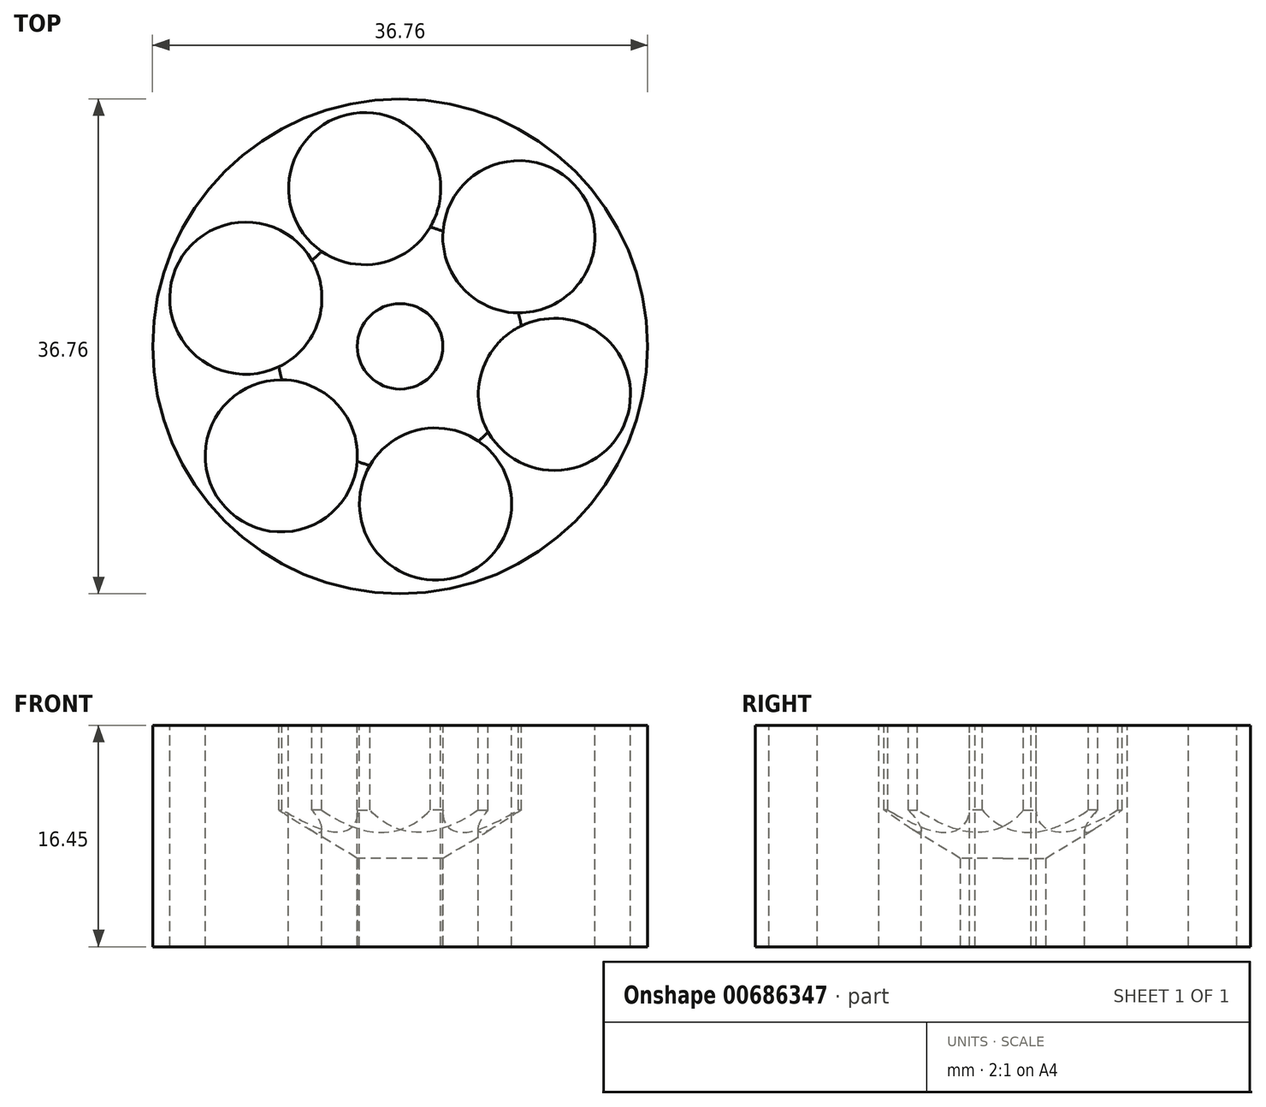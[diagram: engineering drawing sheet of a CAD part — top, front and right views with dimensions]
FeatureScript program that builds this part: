
annotation { "Feature Type Name" : "Feature", "Feature Type Description" : "" }
export const myFeature = defineFeature(function(context is Context, id is Id, definition is map)
    precondition{}
    {
        {
            var Q0;
            Q0=qCreatedBy(makeId("Top.planeOp"),FACE);
            var sketch = newSketch(context, id + "F0", { "sketchPlane" : qUnion([Q0])});
            skCircle(sketch, "E0", {"center": v(0, 0) * mm, "radius": 18.38 * mm});
            skSolve(sketch);
        }
        {
            var Q0;
            Q0=makeQuery(id+"F0.imprint","IMPRINT",FACE,{"disambiguationData":[TD([[makeQuery(id+"F0.imprint","IMPRINT",EDGE,{"derivedFrom":sQuery(id+"F0.wireOp",EDGE,"E0")}),1.0]])]});
            extrude(context, id + "F1", {"entities" : qUnion([Q0]), "depth" : 16.45 * mm, "offsetDistance" : 25.4 * mm});
        }
        {
            var Q0;
            Q0=makeQuery(id+"F1.opExtrude","CAP_FACE",FACE,{"disambiguationData":[OSD([sQuery(id+"F0.wireOp",EDGE,"E0")])],"isStart":false});
            var sketch = newSketch(context, id + "F2", { "sketchPlane" : qUnion([Q0])});
            skCircle(sketch, "E1", {"center": v(0, 0) * mm, "radius": 12 * mm, "construction": true});
            skCircle(sketch, "E2", {"center": v(-11.46, 3.57) * mm, "radius": 4.63 * mm});
            skCircle(sketch, "E3.1.0", {"center": v(-8.82, -8.13) * mm, "radius": 4.63 * mm});
            skCircle(sketch, "E3.2.0", {"center": v(2.63, -11.7) * mm, "radius": 4.63 * mm});
            skCircle(sketch, "E3.3.0", {"center": v(11.46, -3.57) * mm, "radius": 4.63 * mm});
            skCircle(sketch, "E3.4.0", {"center": v(8.82, 8.13) * mm, "radius": 4.63 * mm});
            skCircle(sketch, "E3.5.0", {"center": v(-2.63, 11.7) * mm, "radius": 4.63 * mm});
            skSolve(sketch);
        }
        {
            var Q0;
            Q0=sQuery(id+"F2.wireOp",VERTEX,"E3.1.0.center");
            var Q1;
            Q1=sQuery(id+"F2.wireOp",VERTEX,"E3.5.0.center");
            var Q2;
            Q2=sQuery(id+"F2.wireOp",VERTEX,"E2.center");
            var Q3;
            Q3=sQuery(id+"F2.wireOp",VERTEX,"E3.2.0.center");
            var Q4;
            Q4=sQuery(id+"F2.wireOp",VERTEX,"E3.3.0.center");
            var Q5;
            Q5=sQuery(id+"F2.wireOp",VERTEX,"E3.4.0.center");
            var Q6;
            Q6=makeQuery(id+"F1.opExtrude","SWEPT_BODY",BODY,{"disambiguationData":[OSD([sQuery(id+"F0.wireOp",EDGE,"E0")])]});
            hole(context, id + "F3", {"style" : HoleStyle.SIMPLE, "endStyle" : HoleEndStyle.THROUGH, "holeDiameter" : 11.3 * mm, "majorDiameter" : 6.35 * mm, "isTappedThrough" : true, "tappedDepth" : 12.7 * mm, "tapClearance" : 3, "locations" : qUnion([Q0, Q1, Q2, Q3, Q4, Q5]), "scope" : qUnion([Q6])});
        }
        {
            var Q0;
            Q0=makeQuery(id+"F1.opExtrude","CAP_FACE",FACE,{"disambiguationData":[OSD([sQuery(id+"F0.wireOp",EDGE,"E0")])],"isStart":false});
            var sketch = newSketch(context, id + "F4", { "sketchPlane" : qUnion([Q0])});
            skPoint(sketch, "E4", {"position": v(0, 0) * mm});
            skSolve(sketch);
        }
        {
            var Q0;
            Q0=sQuery(id+"F4.wireOp",VERTEX,"E4");
            var Q1;
            Q1=makeQuery(id+"F1.opExtrude","SWEPT_BODY",BODY,{"disambiguationData":[OSD([sQuery(id+"F0.wireOp",EDGE,"E0")])]});
            hole(context, id + "F5", {"style" : HoleStyle.SIMPLE, "endStyle" : HoleEndStyle.BLIND, "holeDiameter" : 18.25 * mm, "majorDiameter" : 6.35 * mm, "holeDepth" : 6.3 * mm, "isTappedThrough" : true, "tappedDepth" : 12.7 * mm, "tapClearance" : 3, "startFromSketch" : true, "locations" : qUnion([Q0]), "scope" : qUnion([Q1])});
        }
        {
            var Q0;
            Q0=makeQuery(id+"F1.opExtrude","CAP_FACE",FACE,{"disambiguationData":[OSD([sQuery(id+"F0.wireOp",EDGE,"E0")])],"isStart":true});
            var sketch = newSketch(context, id + "F6", { "sketchPlane" : qUnion([Q0])});
            skPoint(sketch, "E5", {"position": v(0, 0) * mm});
            skSolve(sketch);
        }
        {
            var Q0;
            Q0=sQuery(id+"F6.wireOp",VERTEX,"E5");
            var Q1;
            Q1=makeQuery(id+"F1.opExtrude","SWEPT_BODY",BODY,{"disambiguationData":[OSD([sQuery(id+"F0.wireOp",EDGE,"E0")])]});
            hole(context, id + "F7", {"style" : HoleStyle.SIMPLE, "endStyle" : HoleEndStyle.THROUGH, "holeDiameter" : 6.35 * mm, "majorDiameter" : 6.35 * mm, "isTappedThrough" : true, "tappedDepth" : 12.7 * mm, "tapClearance" : 3, "startFromSketch" : true, "locations" : qUnion([Q0]), "scope" : qUnion([Q1])});
        }
    });
